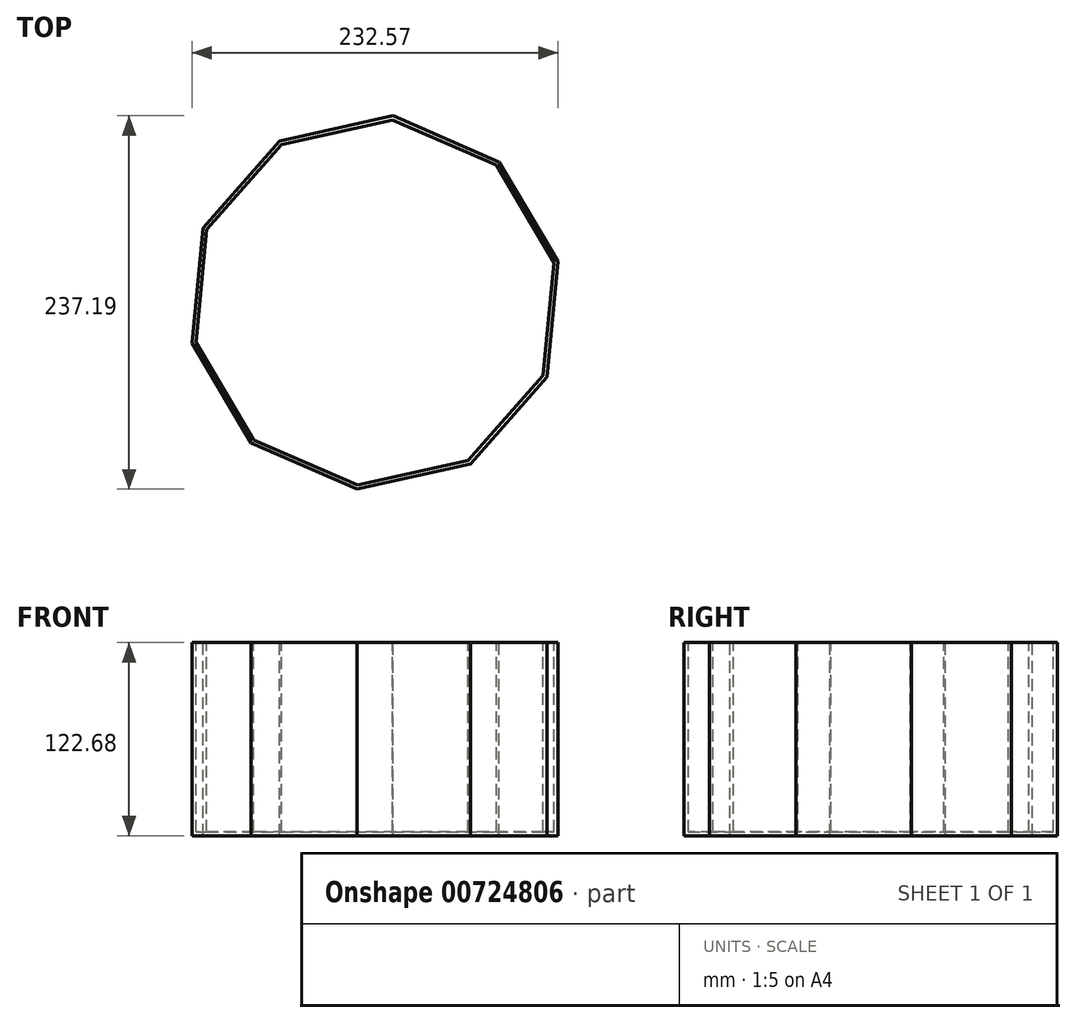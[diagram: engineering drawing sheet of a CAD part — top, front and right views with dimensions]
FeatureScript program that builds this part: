
annotation { "Feature Type Name" : "Feature", "Feature Type Description" : "" }
export const myFeature = defineFeature(function(context is Context, id is Id, definition is map)
    precondition{}
    {
        {
            var Q0;
            Q0=qCreatedBy(makeId("Top.planeOp"),FACE);
            var sketch = newSketch(context, id + "F0", { "sketchPlane" : qUnion([Q0])});
            skCircle(sketch, "E0.cCircle", {"center": v(-98.95, 5.76) * mm, "radius": 113.3 * mm, "construction": true});
            skLineSegment(sketch, "E0.0", {"start": v(10.35, -41.64) * mm, "end": v(-38.38, -96.84) * mm});
            skLineSegment(sketch, "E0.1", {"start": v(-38.38, -96.84) * mm, "end": v(-110.25, -112.84) * mm});
            skLineSegment(sketch, "E0.2", {"start": v(-110.25, -112.84) * mm, "end": v(-177.8, -83.55) * mm});
            skLineSegment(sketch, "E0.3", {"start": v(-177.8, -83.55) * mm, "end": v(-215.23, -20.14) * mm});
            skLineSegment(sketch, "E0.4", {"start": v(-215.23, -20.14) * mm, "end": v(-208.25, 53.15) * mm});
            skLineSegment(sketch, "E0.5", {"start": v(-208.25, 53.15) * mm, "end": v(-159.51, 108.35) * mm});
            skLineSegment(sketch, "E0.6", {"start": v(-159.51, 108.35) * mm, "end": v(-87.64, 124.35) * mm});
            skLineSegment(sketch, "E0.7", {"start": v(-87.64, 124.35) * mm, "end": v(-20.1, 95.06) * mm});
            skLineSegment(sketch, "E0.8", {"start": v(-20.1, 95.06) * mm, "end": v(17.34, 31.65) * mm});
            skLineSegment(sketch, "E0.9", {"start": v(17.34, 31.65) * mm, "end": v(10.35, -41.64) * mm});
            skPoint(sketch, "E0.0.midPoint", {"position": v(-14.02, -69.24) * mm});
            skSolve(sketch);
        }
        {
            var Q0;
            Q0=makeQuery(id+"F0.imprint","IMPRINT",FACE,{"disambiguationData":[TD([[makeQuery(id+"F0.imprint","IMPRINT",EDGE,{"derivedFrom":sQuery(id+"F0.wireOp",EDGE,"E0.0")}),-1.0]])]});
            extrude(context, id + "F1", {"entities" : qUnion([Q0]), "oppositeDirection" : true, "depth" : 122.68 * mm, "offsetDistance" : 25.4 * mm});
        }
        {
            var Q0;
            Q0=makeQuery(id+"F1.opExtrude","CAP_FACE",FACE,{"disambiguationData":[OSD([sQuery(id+"F0.wireOp",EDGE,"E0.0"),sQuery(id+"F0.wireOp",EDGE,"E0.1"),sQuery(id+"F0.wireOp",EDGE,"E0.2"),sQuery(id+"F0.wireOp",EDGE,"E0.3"),sQuery(id+"F0.wireOp",EDGE,"E0.4"),sQuery(id+"F0.wireOp",EDGE,"E0.5"),sQuery(id+"F0.wireOp",EDGE,"E0.6"),sQuery(id+"F0.wireOp",EDGE,"E0.7"),sQuery(id+"F0.wireOp",EDGE,"E0.8"),sQuery(id+"F0.wireOp",EDGE,"E0.9")])],"isStart":true});
            shell(context, id + "F2", {"entities" : qUnion([Q0]), "thickness" : 2.54 * mm});
        }
    });
